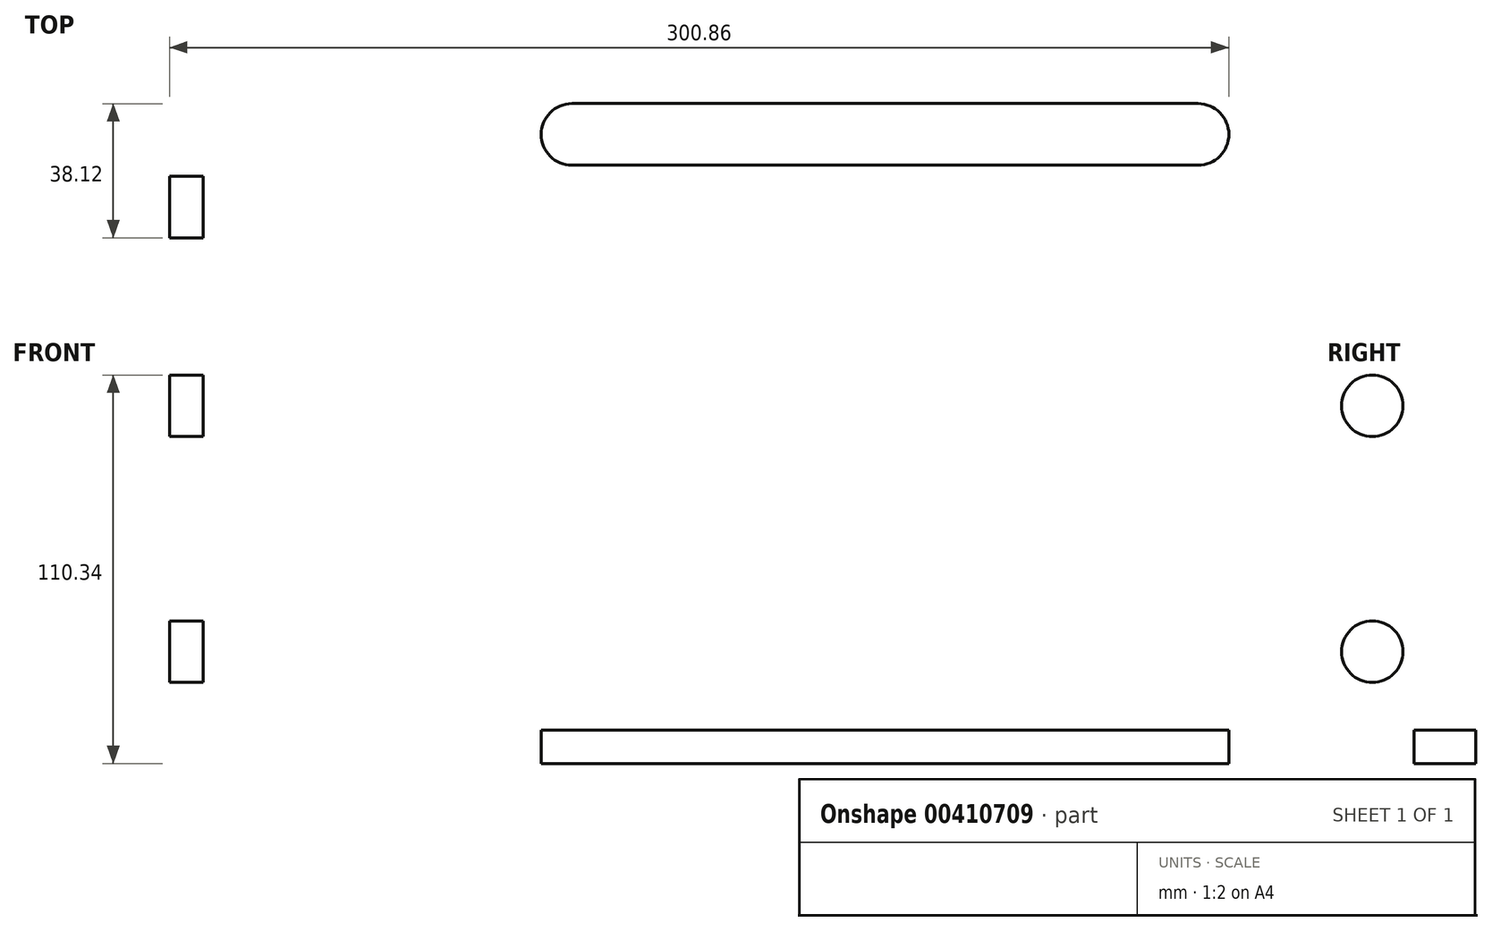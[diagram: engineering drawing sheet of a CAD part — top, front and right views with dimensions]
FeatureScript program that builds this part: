
annotation { "Feature Type Name" : "Feature", "Feature Type Description" : "" }
export const myFeature = defineFeature(function(context is Context, id is Id, definition is map)
    precondition{}
    {
        {
            var Q0;
            Q0=qCreatedBy(makeId("Front.planeOp"),FACE);
            var sketch = newSketch(context, id + "F0", { "sketchPlane" : qUnion([Q0])});
            skLineSegment(sketch, "E0", {"start": v(-203.2, 127) * mm, "end": v(-203.2, 0) * mm});
            skLineSegment(sketch, "E1", {"start": v(-203.2, 0) * mm, "end": v(203.2, 0) * mm});
            skLineSegment(sketch, "E2", {"start": v(-203.2, 127) * mm, "end": v(-193.68, 127) * mm});
            skLineSegment(sketch, "E3", {"start": v(-193.68, 127) * mm, "end": v(-193.68, 9.52) * mm});
            skLineSegment(sketch, "E4", {"start": v(-193.68, 9.52) * mm, "end": v(203.2, 9.53) * mm});
            skLineSegment(sketch, "E5", {"start": v(203.2, 9.53) * mm, "end": v(203.2, 0) * mm});
            skSolve(sketch);
        }
        {
            var Q0;
            Q0 = qSketchRegion(id + "F0", true);
            extrude(context, id + "F1", {"entities" : qUnion([Q0]), "endBound" : BoundingType.SYMMETRIC, "depth" : 76.2 * mm});
        }
        {
            var Q0;
            Q0=makeQuery(id+"F1.opExtrude","CAP_EDGE",EDGE,{"disambiguationData":[OSD([sQuery(id+"F0.wireOp",EDGE,"E2")])],"isStart":false});
            var Q1;
            Q1=makeQuery(id+"F1.opExtrude","CAP_EDGE",EDGE,{"disambiguationData":[OSD([sQuery(id+"F0.wireOp",EDGE,"E2")])],"isStart":true});
            var Q2;
            Q2=makeQuery(id+"F1.opExtrude","CAP_EDGE",EDGE,{"disambiguationData":[OSD([sQuery(id+"F0.wireOp",EDGE,"E5")])],"isStart":false});
            var Q3;
            Q3=makeQuery(id+"F1.opExtrude","CAP_EDGE",EDGE,{"disambiguationData":[OSD([sQuery(id+"F0.wireOp",EDGE,"E5")])],"isStart":true});
            fillet(context, id + "F2", {"entities" : qUnion([Q0, Q1, Q2, Q3]), "radius" : 9.52 * mm, "tangentPropagation" : true, "allowEdgeOverflow" : false});
        }
        {
            var Q0;
            Q0=makeQuery(id+"F1.opExtrude","SWEPT_EDGE",EDGE,{"disambiguationData":[OSD([sQuery(id+"F0.wireOp",EDGE,"E3"),sQuery(id+"F0.wireOp",EDGE,"E4")])]});
            fillet(context, id + "F3", {"entities" : qUnion([Q0]), "radius" : 3.17 * mm, "tangentPropagation" : true, "allowEdgeOverflow" : false});
        }
        {
            var Q0;
            Q0=makeQuery(id+"F1.opExtrude","SWEPT_EDGE",EDGE,{"disambiguationData":[OSD([sQuery(id+"F0.wireOp",EDGE,"E0"),sQuery(id+"F0.wireOp",EDGE,"E1")])]});
            fillet(context, id + "F4", {"entities" : qUnion([Q0]), "radius" : 9.52 * mm, "tangentPropagation" : true, "allowEdgeOverflow" : false});
        }
        {
            var Q0;
            Q0=makeQuery(id+"F1.opExtrude","SWEPT_FACE",FACE,{"disambiguationData":[OSD([sQuery(id+"F0.wireOp",EDGE,"E0")])]});
            var sketch = newSketch(context, id + "F5", { "sketchPlane" : qUnion([Q0])});
            skLineSegment(sketch, "E6", {"start": v(0, 127) * mm, "end": v(0, 9.53) * mm, "construction": true});
            skCircle(sketch, "E7", {"center": v(-20.62, 101.6) * mm, "radius": 8.74 * mm});
            skCircle(sketch, "E8", {"center": v(-20.62, 31.75) * mm, "radius": 8.74 * mm});
            skCircle(sketch, "E9.MirrorC", {"center": v(20.62, 101.6) * mm, "radius": 8.74 * mm});
            skCircle(sketch, "E10.MirrorC", {"center": v(20.62, 31.75) * mm, "radius": 8.74 * mm});
            skSolve(sketch);
        }
        {
            var Q0;
            Q0=makeQuery(id+"F5.imprint","IMPRINT",FACE,{"disambiguationData":[TD([[makeQuery(id+"F5.imprint","IMPRINT",EDGE,{"derivedFrom":sQuery(id+"F5.wireOp",EDGE,"E9.MirrorC")}),-1.0]])]});
            var Q1;
            Q1=makeQuery(id+"F5.imprint","IMPRINT",FACE,{"disambiguationData":[TD([[makeQuery(id+"F5.imprint","IMPRINT",EDGE,{"derivedFrom":sQuery(id+"F5.wireOp",EDGE,"E8")}),1.0]])]});
            var Q2;
            Q2=makeQuery(id+"F5.imprint","IMPRINT",FACE,{"disambiguationData":[TD([[makeQuery(id+"F5.imprint","IMPRINT",EDGE,{"derivedFrom":sQuery(id+"F5.wireOp",EDGE,"E10.MirrorC")}),-1.0]])]});
            var Q3;
            Q3=makeQuery(id+"F5.imprint","IMPRINT",FACE,{"disambiguationData":[TD([[makeQuery(id+"F5.imprint","IMPRINT",EDGE,{"derivedFrom":sQuery(id+"F5.wireOp",EDGE,"E7")}),1.0]])]});
            var Q4;
            Q4=sQuery(id+"F5.wireOp",EDGE,"E8");
            var Q5;
            Q5=sQuery(id+"F5.wireOp",EDGE,"E10.MirrorC");
            var Q6;
            Q6=sQuery(id+"F5.wireOp",EDGE,"E9.MirrorC");
            var Q7;
            Q7=sQuery(id+"F5.wireOp",EDGE,"E7");
            extrude(context, id + "F6", {"entities" : qUnion([Q0, Q1, Q2, Q3]), "operationType" : NewBodyOperationType.REMOVE, "surfaceEntities" : qUnion([Q4, Q5, Q6, Q7]), "oppositeDirection" : true, "depth" : 25.4 * mm});
        }
        {
            var Q0;
            Q0=makeQuery(id+"F1.opExtrude","SWEPT_FACE",FACE,{"disambiguationData":[OSD([sQuery(id+"F0.wireOp",EDGE,"E4")])]});
            var sketch = newSketch(context, id + "F7", { "sketchPlane" : qUnion([Q0])});
            skLineSegment(sketch, "E11", {"start": v(-190.5, 0) * mm, "end": v(203.2, 0) * mm, "construction": true});
            skLineSegment(sketch, "E12", {"start": v(-88.9, 0) * mm, "end": v(88.9, 0) * mm});
            skArc(sketch, "E13.0.startCap", {"start": v(-88.9, -8.76) * mm, "mid": v(-97.66, 0) * mm, "end": v(-88.9, 8.76) * mm});
            skArc(sketch, "E13.0.endCap", {"start": v(88.9, 8.76) * mm, "mid": v(97.66, 0) * mm, "end": v(88.9, -8.76) * mm});
            skLineSegment(sketch, "E13.0.left", {"start": v(-88.9, 8.76) * mm, "end": v(88.9, 8.76) * mm});
            skLineSegment(sketch, "E13.0.right", {"start": v(-88.9, -8.76) * mm, "end": v(88.9, -8.76) * mm});
            skPoint(sketch, "E14", {"position": v(0, 0) * mm});
            skSolve(sketch);
        }
        {
            var Q0;
            Q0=makeQuery(id+"F7.imprint","IMPRINT",FACE,{"disambiguationData":[TD([[makeQuery(id+"F7.imprint","IMPRINT",EDGE,{"derivedFrom":sQuery(id+"F7.wireOp",EDGE,"E13.0.startCap")}),-1.0]])]});
            var Q1;
            Q1=sQuery(id+"F7.wireOp",EDGE,"E13.0.startCap");
            var Q2;
            Q2=sQuery(id+"F7.wireOp",EDGE,"E13.0.left");
            var Q3;
            Q3=sQuery(id+"F7.wireOp",EDGE,"E13.0.right");
            var Q4;
            Q4=sQuery(id+"F7.wireOp",EDGE,"E13.0.endCap");
            extrude(context, id + "F8", {"entities" : qUnion([Q0]), "operationType" : NewBodyOperationType.REMOVE, "surfaceEntities" : qUnion([Q1, Q2, Q3, Q4]), "oppositeDirection" : true, "depth" : 25.4 * mm});
        }
    });
